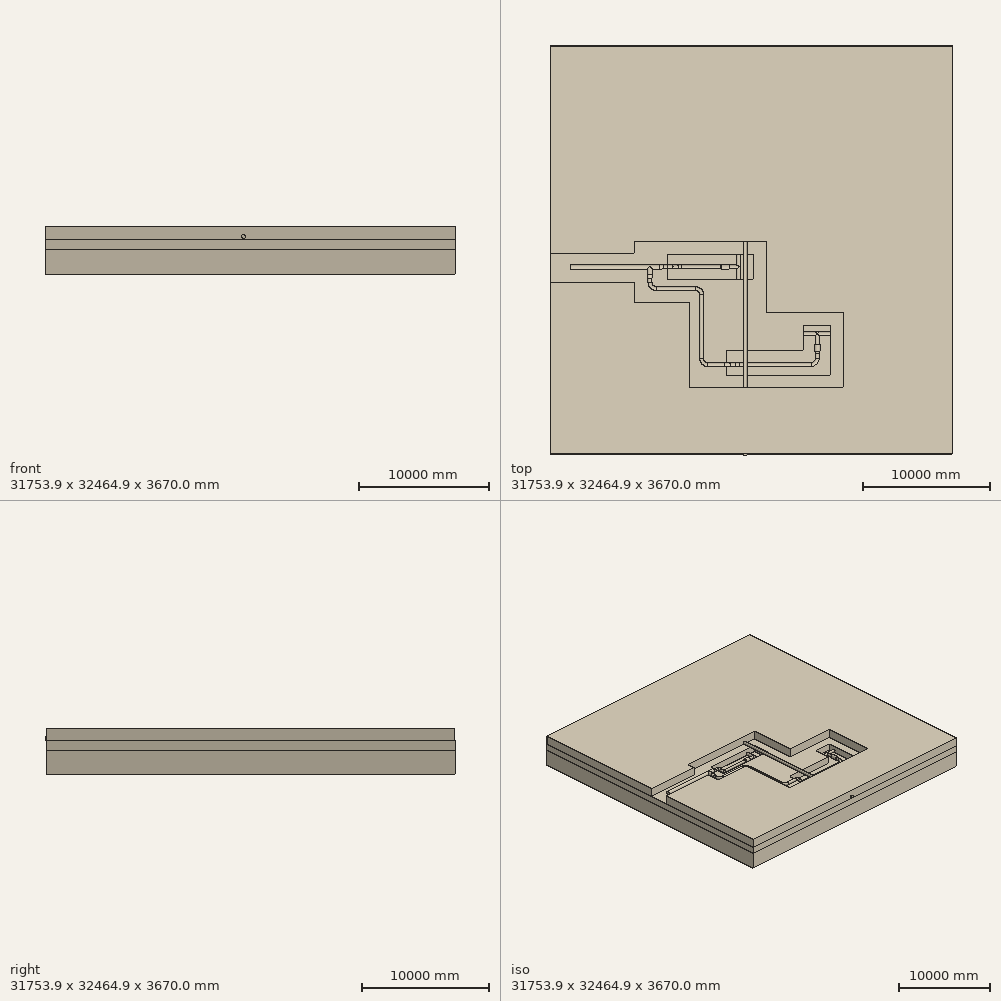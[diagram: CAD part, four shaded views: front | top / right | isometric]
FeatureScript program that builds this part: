
annotation { "Feature Type Name" : "Feature", "Feature Type Description" : "" }
export const myFeature = defineFeature(function(context is Context, id is Id, definition is map)
    precondition{}
    {
        {
            var Q0;
            Q0=qCreatedBy(makeId("Front.planeOp"),FACE);
            var sketch = newSketch(context, id + "F0", { "sketchPlane" : qUnion([Q0])});
            skCircle(sketch, "E0", {"center": v(0, 0) * mm, "radius": 157.5 * mm});
            skSolve(sketch);
        }
        {
            var Q0;
            Q0=qCreatedBy(makeId("Right.planeOp"),FACE);
            var sketch = newSketch(context, id + "F1", { "sketchPlane" : qUnion([Q0])});
            skLineSegment(sketch, "E1", {"start": v(0, 0) * mm, "end": v(-1158.97, 0) * mm});
            skLineSegment(sketch, "E2", {"start": v(-1512.52, -146.45) * mm, "end": v(-2019.63, -653.55) * mm});
            skLineSegment(sketch, "E3", {"start": v(-2373.18, -800) * mm, "end": v(-22166.07, -800) * mm});
            skPoint(sketch, "E4.visualSharp", {"position": v(-2166.07, -800) * mm});
            skArc(sketch, "E4.filletArc", {"start": v(-2373.18, -800) * mm, "mid": v(-2181.84, -761.94) * mm, "end": v(-2019.63, -653.55) * mm});
            skPoint(sketch, "E5.visualSharp", {"position": v(-1366.07, 0) * mm});
            skArc(sketch, "E5.filletArc", {"start": v(-1158.97, 0) * mm, "mid": v(-1350.3, -38.06) * mm, "end": v(-1512.52, -146.45) * mm});
            skSolve(sketch);
        }
        {
            var Q0;
            Q0=qSketchRegion(id+"F0",true);
            var Q1;
            Q1=qConstructionFilter(qBodyType(qCreatedBy(id+"F1",EDGE),BodyType.WIRE),ConstructionObject.NO);
            sweep(context, id + "F2", {"profiles" : qUnion([Q0]), "path" : qUnion([Q1])});
        }
        {
            var Q0;
            Q0=qCreatedBy(makeId("Front.planeOp"),FACE);
            var sketch = newSketch(context, id + "F3", { "sketchPlane" : qUnion([Q0])});
            skCircle(sketch, "E6", {"center": v(500, 0) * mm, "radius": 157.5 * mm});
            skSolve(sketch);
        }
        {
            var Q0;
            Q0=qSketchRegion(id+"F3",true);
            extrude(context, id + "F4", {"entities" : qUnion([Q0]), "depth" : 31800 * mm, "offsetDistance" : 25 * mm});
        }
        {
            var Q0;
            Q0=qCreatedBy(makeId("Right.planeOp"),FACE);
            var sketch = newSketch(context, id + "F5", { "sketchPlane" : qUnion([Q0])});
            skCircle(sketch, "E7", {"center": v(-22166, -800) * mm, "radius": 157.5 * mm});
            skSolve(sketch);
        }
        {
            var Q0;
            Q0=qCreatedBy(makeId("Right.planeOp"),FACE);
            cPlane(context, id + "F6", {"entities" : qUnion([Q0]), "cplaneType" : CPlaneType.OFFSET, "offset" : 16000 * mm, "width" : 150 * mm, "height" : 150 * mm});
        }
        {
            var Q0;
            Q0=qCreatedBy(id+"F6.planeOp",FACE);
            var sketch = newSketch(context, id + "F7", { "sketchPlane" : qUnion([Q0])});
            skCircle(sketch, "E8", {"center": v(-21525.22, 0) * mm, "radius": 157.5 * mm});
            skSolve(sketch);
        }
        {
            var Q0;
            Q0=qCreatedBy(makeId("Front.planeOp"),FACE);
            var Q1;
            Q1=sQuery(id+"F7.wireOp",VERTEX,"E8.center");
            cPlane(context, id + "F8", {"entities" : qUnion([Q0, Q1]), "cplaneType" : CPlaneType.PLANE_POINT, "offset" : 25 * mm, "width" : 150 * mm, "height" : 150 * mm});
        }
        {
            var Q0;
            Q0=qCreatedBy(id+"F8.planeOp",FACE);
            var sketch = newSketch(context, id + "F9", { "sketchPlane" : qUnion([Q0])});
            skLineSegment(sketch, "E9", {"start": v(16002.5, 0) * mm, "end": v(14288.3, 0) * mm});
            skLineSegment(sketch, "E10", {"start": v(13967.3, -116.64) * mm, "end": v(12326.43, -1490.56) * mm});
            skLineSegment(sketch, "E11", {"start": v(12005.44, -1607.2) * mm, "end": v(-8115.68, -1607.2) * mm});
            skLineSegment(sketch, "E12", {"start": v(-8532.64, -1383.14) * mm, "end": v(-9299.71, -224.06) * mm});
            skLineSegment(sketch, "E13", {"start": v(-9716.67, 0) * mm, "end": v(-13355.66, 0) * mm});
            skPoint(sketch, "E14.visualSharp", {"position": v(14106.6, 0) * mm});
            skArc(sketch, "E14.filletArc", {"start": v(14288.3, 0) * mm, "mid": v(14117.53, -30.06) * mm, "end": v(13967.3, -116.64) * mm});
            skPoint(sketch, "E15.visualSharp", {"position": v(12187.13, -1607.2) * mm});
            skArc(sketch, "E15.filletArc", {"start": v(12005.44, -1607.2) * mm, "mid": v(12176.2, -1577.13) * mm, "end": v(12326.43, -1490.56) * mm});
            skPoint(sketch, "E16.visualSharp", {"position": v(-9448, 0) * mm});
            skArc(sketch, "E16.filletArc", {"start": v(-9299.71, -224.06) * mm, "mid": v(-9480, -59.56) * mm, "end": v(-9716.67, 0) * mm});
            skPoint(sketch, "E17.visualSharp", {"position": v(-8384.36, -1607.2) * mm});
            skArc(sketch, "E17.filletArc", {"start": v(-8532.64, -1383.14) * mm, "mid": v(-8352.35, -1547.63) * mm, "end": v(-8115.68, -1607.2) * mm});
            skSolve(sketch);
        }
        {
            var Q0;
            Q0=qSketchRegion(id+"F7",true);
            var Q1;
            Q1=qConstructionFilter(qBodyType(qCreatedBy(id+"F9",EDGE),BodyType.WIRE),ConstructionObject.NO);
            sweep(context, id + "F10", {"profiles" : qUnion([Q0]), "path" : qUnion([Q1])});
        }
        {
            var Q0;
            Q0=qCreatedBy(id+"F6.planeOp",FACE);
            var sketch = newSketch(context, id + "F11", { "sketchPlane" : qUnion([Q0])});
            skCircle(sketch, "E18", {"center": v(-22166, 0) * mm, "radius": 157.5 * mm});
            skSolve(sketch);
        }
        {
            var Q0;
            Q0=qCreatedBy(makeId("Front.planeOp"),FACE);
            var Q1;
            Q1=sQuery(id+"F11.wireOp",VERTEX,"E18.center");
            cPlane(context, id + "F12", {"entities" : qUnion([Q0, Q1]), "cplaneType" : CPlaneType.PLANE_POINT, "offset" : 25 * mm, "width" : 150 * mm, "height" : 150 * mm});
        }
        {
            var Q0;
            Q0=qCreatedBy(id+"F12.planeOp",FACE);
            var sketch = newSketch(context, id + "F13", { "sketchPlane" : qUnion([Q0])});
            skLineSegment(sketch, "E19", {"start": v(16049.86, 0) * mm, "end": v(14213.99, 0) * mm});
            skLineSegment(sketch, "E20", {"start": v(13860.44, -146.45) * mm, "end": v(13353.33, -653.55) * mm});
            skLineSegment(sketch, "E21", {"start": v(12999.78, -800) * mm, "end": v(0, -800) * mm});
            skLineSegment(sketch, "E22", {"start": v(0, -800) * mm, "end": v(-8588.31, -800) * mm});
            skLineSegment(sketch, "E23", {"start": v(-8941.87, -653.55) * mm, "end": v(-9448.97, -146.45) * mm});
            skLineSegment(sketch, "E24", {"start": v(-9802.53, 0) * mm, "end": v(-13399.06, 0) * mm});
            skPoint(sketch, "E25.visualSharp", {"position": v(14006.88, 0) * mm});
            skArc(sketch, "E25.filletArc", {"start": v(14213.99, 0) * mm, "mid": v(14022.65, -38.06) * mm, "end": v(13860.44, -146.45) * mm});
            skPoint(sketch, "E26.visualSharp", {"position": v(13206.88, -800) * mm});
            skArc(sketch, "E26.filletArc", {"start": v(12999.78, -800) * mm, "mid": v(13191.12, -761.94) * mm, "end": v(13353.33, -653.55) * mm});
            skPoint(sketch, "E27.visualSharp", {"position": v(-8795.42, -800) * mm});
            skArc(sketch, "E27.filletArc", {"start": v(-8941.87, -653.55) * mm, "mid": v(-8779.66, -761.94) * mm, "end": v(-8588.31, -800) * mm});
            skPoint(sketch, "E28.visualSharp", {"position": v(-9595.42, 0) * mm});
            skArc(sketch, "E28.filletArc", {"start": v(-9448.97, -146.45) * mm, "mid": v(-9611.19, -38.06) * mm, "end": v(-9802.53, 0) * mm});
            skSolve(sketch);
        }
        {
            var Q0;
            Q0=qSketchRegion(id+"F11",true);
            var Q1;
            Q1=qConstructionFilter(qBodyType(qCreatedBy(id+"F13",EDGE),BodyType.WIRE),ConstructionObject.NO);
            sweep(context, id + "F14", {"operationType" : NewBodyOperationType.ADD, "profiles" : qUnion([Q0]), "path" : qUnion([Q1])});
        }
        {
            var Q0;
            Q0=makeQuery(id+"F10.opSweep","CAP_FACE",FACE,{"disambiguationData":[OSD([sQuery(id+"F7.wireOp",EDGE,"E8"),sQuery(id+"F9.wireOp",VERTEX,"E13.end")])],"isStart":true});
            var sketch = newSketch(context, id + "F15", { "sketchPlane" : qUnion([Q0])});
            skCircle(sketch, "E29", {"center": v(16867.72, 0) * mm, "radius": 225 * mm});
            skSolve(sketch);
        }
        {
            var Q0;
            Q0=qSketchRegion(id+"F15",true);
            extrude(context, id + "F16", {"entities" : qUnion([Q0]), "oppositeDirection" : true, "depth" : 7050 * mm, "offsetDistance" : 25 * mm});
        }
        {
            var Q0;
            Q0=makeQuery(id+"F16.opExtrude","CAP_FACE",FACE,{"disambiguationData":[OSD([sQuery(id+"F15.wireOp",EDGE,"E29")])],"isStart":false});
            var sketch = newSketch(context, id + "F17", { "sketchPlane" : qUnion([Q0])});
            skCircle(sketch, "E30", {"center": v(-16867.72, 0) * mm, "radius": 225 * mm});
            skSolve(sketch);
        }
        {
            var Q0;
            Q0=makeQuery(id+"F17.imprint","IMPRINT",FACE,{"disambiguationData":[TD([[makeQuery(id+"F17.imprint","IMPRINT",EDGE,{"derivedFrom":sQuery(id+"F17.wireOp",EDGE,"E30")}),-1.0]])]});
            cPlane(context, id + "F18", {"entities" : qUnion([Q0]), "cplaneType" : CPlaneType.OFFSET, "offset" : 343 * mm, "width" : 150 * mm, "height" : 150 * mm});
        }
        {
            var Q0;
            Q0=qCreatedBy(id+"F18.planeOp",FACE);
            var sketch = newSketch(context, id + "F19", { "sketchPlane" : qUnion([Q0])});
            skCircle(sketch, "E31", {"center": v(-16868.24, -67.5) * mm, "radius": 157.5 * mm});
            skSolve(sketch);
        }
        {
            var Q0;
            Q0=qSketchRegion(id+"F17",true);
            var Q1;
            Q1=qSketchRegion(id+"F19",true);
            loft(context, id + "F20", {"operationType" : NewBodyOperationType.ADD, "sheetProfilesArray" : [{ "sheetProfileEntities" : qUnion([Q0]) }, { "sheetProfileEntities" : qUnion([Q1]) }]});
        }
        {
            var Q0;
            Q0=qCreatedBy(makeId("Front.planeOp"),FACE);
            var Q1;
            Q1=sQuery(id+"F15.wireOp",VERTEX,"E29.center");
            cPlane(context, id + "F21", {"entities" : qUnion([Q0, Q1]), "cplaneType" : CPlaneType.PLANE_POINT, "offset" : 25 * mm, "width" : 150 * mm, "height" : 150 * mm});
        }
        {
            var Q0;
            Q0=qCreatedBy(id+"F21.planeOp",FACE);
            var sketch = newSketch(context, id + "F22", { "sketchPlane" : qUnion([Q0])});
            skLineSegment(sketch, "E32", {"start": v(-5962.66, -83.9) * mm, "end": v(-5669.76, -83.9) * mm});
            skLineSegment(sketch, "E33", {"start": v(-5316.21, -230.35) * mm, "end": v(-4893, -653.55) * mm});
            skLineSegment(sketch, "E34", {"start": v(-4539.45, -800) * mm, "end": v(-1450, -800) * mm});
            skPoint(sketch, "E35.visualSharp", {"position": v(-5462.66, -83.9) * mm});
            skArc(sketch, "E35.filletArc", {"start": v(-5316.21, -230.35) * mm, "mid": v(-5478.42, -121.96) * mm, "end": v(-5669.76, -83.9) * mm});
            skPoint(sketch, "E36.visualSharp", {"position": v(-4746.56, -800) * mm});
            skArc(sketch, "E36.filletArc", {"start": v(-4893, -653.55) * mm, "mid": v(-4730.8, -761.94) * mm, "end": v(-4539.45, -800) * mm});
            skSolve(sketch);
        }
        {
            var Q0;
            Q0=qSketchRegion(id+"F19",true);
            var Q1;
            Q1=qConstructionFilter(qBodyType(qCreatedBy(id+"F22",EDGE),BodyType.WIRE),ConstructionObject.NO);
            sweep(context, id + "F23", {"operationType" : NewBodyOperationType.ADD, "profiles" : qUnion([Q0]), "path" : qUnion([Q1])});
        }
        {
            var Q0;
            Q0=makeQuery(id+"F23.opSweep","CAP_FACE",FACE,{"disambiguationData":[OSD([sQuery(id+"F19.wireOp",EDGE,"E31"),sQuery(id+"F22.wireOp",VERTEX,"E34.end")])],"isStart":false});
            var sketch = newSketch(context, id + "F24", { "sketchPlane" : qUnion([Q0])});
            skCircle(sketch, "E37", {"center": v(-16868.24, -783.6) * mm, "radius": 157.5 * mm});
            skSolve(sketch);
        }
        {
            var Q0;
            Q0=qCreatedBy(makeId("Front.planeOp"),FACE);
            var Q1;
            Q1=sQuery(id+"F24.wireOp",VERTEX,"E37.center");
            cPlane(context, id + "F25", {"entities" : qUnion([Q0, Q1]), "cplaneType" : CPlaneType.PLANE_POINT, "offset" : 25 * mm, "width" : 150 * mm, "height" : 150 * mm});
        }
        {
            var Q0;
            Q0=qCreatedBy(id+"F25.planeOp",FACE);
            var sketch = newSketch(context, id + "F26", { "sketchPlane" : qUnion([Q0])});
            skCircle(sketch, "E38", {"center": v(-7026.1, 0) * mm, "radius": 225 * mm});
            skSolve(sketch);
        }
        {
            var Q0;
            Q0=qSketchRegion(id+"F26",true);
            extrude(context, id + "F27", {"entities" : qUnion([Q0]), "operationType" : NewBodyOperationType.ADD, "depth" : 610 * mm, "offsetDistance" : 25 * mm});
        }
        {
            var Q0;
            Q0=makeQuery(id+"F27.opExtrude","CAP_FACE",FACE,{"disambiguationData":[OSD([sQuery(id+"F26.wireOp",EDGE,"E38")])],"isStart":false});
            var sketch = newSketch(context, id + "F28", { "sketchPlane" : qUnion([Q0])});
            skCircle(sketch, "E39", {"center": v(-7026.1, 0) * mm, "radius": 225 * mm});
            skSolve(sketch);
        }
        {
            var Q0;
            Q0=makeQuery(id+"F28.imprint","IMPRINT",FACE,{"disambiguationData":[TD([[makeQuery(id+"F28.imprint","IMPRINT",EDGE,{"derivedFrom":sQuery(id+"F28.wireOp",EDGE,"E39")}),1.0]])]});
            cPlane(context, id + "F29", {"entities" : qUnion([Q0]), "cplaneType" : CPlaneType.OFFSET, "offset" : 300 * mm, "width" : 150 * mm, "height" : 150 * mm});
        }
        {
            var Q0;
            Q0=qCreatedBy(id+"F29.planeOp",FACE);
            var sketch = newSketch(context, id + "F30", { "sketchPlane" : qUnion([Q0])});
            skCircle(sketch, "E40", {"center": v(-7026.1, -68) * mm, "radius": 157.5 * mm});
            skSolve(sketch);
        }
        {
            var Q0;
            Q0=qSketchRegion(id+"F28",true);
            var Q1;
            Q1=qSketchRegion(id+"F30",true);
            loft(context, id + "F31", {"operationType" : NewBodyOperationType.ADD, "sheetProfilesArray" : [{ "sheetProfileEntities" : qUnion([Q0]) }, { "sheetProfileEntities" : qUnion([Q1]) }]});
        }
        {
            var Q0;
            Q0=qCreatedBy(id+"F29.planeOp",FACE);
            var sketch = newSketch(context, id + "F32", { "sketchPlane" : qUnion([Q0])});
            skCircle(sketch, "E41", {"center": v(-7028.94, -67.68) * mm, "radius": 157.5 * mm});
            skSolve(sketch);
        }
        {
            var Q0;
            Q0=makeQuery(id+"F31.opLoft","CAP_FACE",FACE,{"disambiguationData":[OSD([makeQuery(id+"F30.imprint","IMPRINT",FACE,{"disambiguationData":[TD([[makeQuery(id+"F30.imprint","IMPRINT",EDGE,{"derivedFrom":sQuery(id+"F30.wireOp",EDGE,"E40")}),1.0]])]})])],"isStart":true});
            var sketch = newSketch(context, id + "F33", { "sketchPlane" : qUnion([Q0])});
            skCircle(sketch, "E42", {"center": v(-7027.04, -67.76) * mm, "radius": 157.5 * mm});
            skSolve(sketch);
        }
        {
            var Q0;
            Q0=qCreatedBy(makeId("Top.planeOp"),FACE);
            var Q1;
            Q1=sQuery(id+"F33.wireOp",VERTEX,"E42.center");
            cPlane(context, id + "F34", {"entities" : qUnion([Q0, Q1]), "cplaneType" : CPlaneType.PLANE_POINT, "offset" : 25 * mm, "width" : 150 * mm, "height" : 150 * mm});
        }
        {
            var Q0;
            Q0=qCreatedBy(id+"F34.planeOp",FACE);
            var sketch = newSketch(context, id + "F35", { "sketchPlane" : qUnion([Q0])});
            skLineSegment(sketch, "E43", {"start": v(-7027.04, -17778.24) * mm, "end": v(-7027.04, -18080.14) * mm});
            skLineSegment(sketch, "E44", {"start": v(-6527.04, -18580.14) * mm, "end": v(-3436.34, -18580.14) * mm});
            skLineSegment(sketch, "E45", {"start": v(-2936.34, -19080.14) * mm, "end": v(-2936.34, -23104.43) * mm});
            skPoint(sketch, "E46.visualSharp", {"position": v(-7027.04, -18580.14) * mm});
            skArc(sketch, "E46.filletArc", {"start": v(-7027.04, -18080.14) * mm, "mid": v(-6880.6, -18433.69) * mm, "end": v(-6527.04, -18580.14) * mm});
            skPoint(sketch, "E47.visualSharp", {"position": v(-2936.34, -18580.14) * mm});
            skArc(sketch, "E47.filletArc", {"start": v(-2936.34, -19080.14) * mm, "mid": v(-3082.79, -18726.58) * mm, "end": v(-3436.34, -18580.14) * mm});
            skSolve(sketch);
        }
        {
            var Q0;
            Q0 = qSketchRegion(id + "F33", true);
            var Q1;
            Q1 = qConstructionFilter(qBodyType(qCreatedBy(id + "F35" ,EDGE), BodyType.WIRE), ConstructionObject.NO);
            sweep(context, id + "F36", {"operationType" : NewBodyOperationType.ADD, "profiles" : qUnion([Q0]), "path" : qUnion([Q1])});
        }
        {
            var Q0;
            Q0=qCreatedBy(makeId("Top.planeOp"),FACE);
            var Q1;
            Q1=sQuery(id+"F32.wireOp",VERTEX,"E41.center");
            cPlane(context, id + "F37", {"entities" : qUnion([Q0, Q1]), "cplaneType" : CPlaneType.PLANE_POINT, "offset" : 25 * mm, "width" : 150 * mm, "height" : 150 * mm});
        }
        {
            var Q0;
            Q0=qCreatedBy(id+"F37.planeOp",FACE);
            var sketch = newSketch(context, id + "F38", { "sketchPlane" : qUnion([Q0])});
            skLineSegment(sketch, "E48", {"start": v(-2933.83, -23104.43) * mm, "end": v(-2933.83, -24104.43) * mm});
            skLineSegment(sketch, "E49", {"start": v(-2433.83, -24604.43) * mm, "end": v(-1452.2, -24604.43) * mm});
            skPoint(sketch, "E50.visualSharp", {"position": v(-2952.2, -24604.31) * mm});
            skArc(sketch, "E50.filletArc", {"start": v(-2933.83, -24104.43) * mm, "mid": v(-2787.38, -24457.98) * mm, "end": v(-2433.83, -24604.43) * mm});
            skSolve(sketch);
        }
        {
            var Q0;
            Q0=makeQuery(id+"F36.opSweep","CAP_FACE",FACE,{"disambiguationData":[OSD([sQuery(id+"F33.wireOp",EDGE,"E42"),sQuery(id+"F35.wireOp",VERTEX,"E45.end")])],"isStart":false});
            var sketch = newSketch(context, id + "F39", { "sketchPlane" : qUnion([Q0])});
            skCircle(sketch, "E51", {"center": v(-2936.34, -67.76) * mm, "radius": 157.5 * mm});
            skSolve(sketch);
        }
        {
            var Q0;
            Q0=qSketchRegion(id+"F39",true);
            var Q1;
            Q1=qConstructionFilter(qBodyType(qCreatedBy(id+"F38",EDGE),BodyType.WIRE),ConstructionObject.NO);
            sweep(context, id + "F40", {"operationType" : NewBodyOperationType.ADD, "profiles" : qUnion([Q0]), "path" : qUnion([Q1])});
        }
        {
            var Q0;
            Q0=makeQuery(id+"F40.opSweep","CAP_FACE",FACE,{"disambiguationData":[OSD([sQuery(id+"F38.wireOp",VERTEX,"E49.end"),sQuery(id+"F39.wireOp",EDGE,"pikIjlxL-Iweg-K63M-rDVM-WGOUHQlHPGsE")])],"isStart":false});
            var sketch = newSketch(context, id + "F41", { "sketchPlane" : qUnion([Q0])});
            skCircle(sketch, "E52", {"center": v(-24606.94, -67.76) * mm, "radius": 157.5 * mm});
            skSolve(sketch);
        }
        {
            var Q0;
            Q0=qCreatedBy(makeId("Top.planeOp"),FACE);
            var Q1;
            Q1=sQuery(id+"F41.wireOp",VERTEX,"E52.center");
            cPlane(context, id + "F42", {"entities" : qUnion([Q0, Q1]), "cplaneType" : CPlaneType.PLANE_POINT, "offset" : 25 * mm, "width" : 150 * mm, "height" : 150 * mm});
        }
        {
            var Q0;
            Q0=qCreatedBy(makeId("Front.planeOp"),FACE);
            var Q1;
            Q1=sQuery(id+"F41.wireOp",VERTEX,"E52.center");
            cPlane(context, id + "F43", {"entities" : qUnion([Q0, Q1]), "cplaneType" : CPlaneType.PLANE_POINT, "offset" : 25 * mm, "width" : 150 * mm, "height" : 150 * mm});
        }
        {
            var Q0;
            Q0=qCreatedBy(id+"F43.planeOp",FACE);
            var sketch = newSketch(context, id + "F44", { "sketchPlane" : qUnion([Q0])});
            skLineSegment(sketch, "E53", {"start": v(-1452.2, -67.68) * mm, "end": v(-1121.65, -67.68) * mm});
            skLineSegment(sketch, "E54", {"start": v(-768.1, -214.12) * mm, "end": v(-328.66, -653.55) * mm});
            skLineSegment(sketch, "E55", {"start": v(24.9, -800) * mm, "end": v(4519.07, -800) * mm});
            skPoint(sketch, "E56.visualSharp", {"position": v(-914.54, -67.68) * mm});
            skArc(sketch, "E56.filletArc", {"start": v(-768.1, -214.12) * mm, "mid": v(-930.3, -105.74) * mm, "end": v(-1121.65, -67.68) * mm});
            skPoint(sketch, "E57.visualSharp", {"position": v(-182.22, -800) * mm});
            skArc(sketch, "E57.filletArc", {"start": v(-328.66, -653.55) * mm, "mid": v(-166.45, -761.94) * mm, "end": v(24.9, -800) * mm});
            skSolve(sketch);
        }
        {
            var Q0;
            Q0=qSketchRegion(id+"F41",true);
            var Q1;
            Q1=qConstructionFilter(qBodyType(qCreatedBy(id+"F44",EDGE),BodyType.WIRE),ConstructionObject.NO);
            sweep(context, id + "F45", {"operationType" : NewBodyOperationType.ADD, "profiles" : qUnion([Q0]), "path" : qUnion([Q1])});
        }
        {
            var Q0;
            Q0=makeQuery(id+"F45.opSweep","CAP_FACE",FACE,{"disambiguationData":[OSD([sQuery(id+"F41.wireOp",EDGE,"E52"),sQuery(id+"F44.wireOp",VERTEX,"E55.end")])],"isStart":false});
            var sketch = newSketch(context, id + "F46", { "sketchPlane" : qUnion([Q0])});
            skCircle(sketch, "E58", {"center": v(-24606.94, -800.08) * mm, "radius": 157.5 * mm});
            skSolve(sketch);
        }
        {
            var Q0;
            Q0=qCreatedBy(makeId("Top.planeOp"),FACE);
            var Q1;
            Q1=sQuery(id+"F46.wireOp",VERTEX,"E58.center");
            cPlane(context, id + "F47", {"entities" : qUnion([Q0, Q1]), "cplaneType" : CPlaneType.PLANE_POINT, "offset" : 25 * mm, "width" : 150 * mm, "height" : 150 * mm});
        }
        {
            var Q0;
            Q0=qCreatedBy(id+"F47.planeOp",FACE);
            var sketch = newSketch(context, id + "F48", { "sketchPlane" : qUnion([Q0])});
            skLineSegment(sketch, "E59", {"start": v(4519.07, -24606.94) * mm, "end": v(5727.78, -24606.94) * mm});
            skLineSegment(sketch, "E60", {"start": v(6227.78, -24106.94) * mm, "end": v(6227.78, -23690.58) * mm});
            skPoint(sketch, "E61.visualSharp", {"position": v(6227.78, -24606.94) * mm});
            skArc(sketch, "E61.filletArc", {"start": v(5727.78, -24606.94) * mm, "mid": v(6081.34, -24460.5) * mm, "end": v(6227.78, -24106.94) * mm});
            skSolve(sketch);
        }
        {
            var Q0;
            Q0=qSketchRegion(id+"F46",true);
            var Q1;
            Q1=qConstructionFilter(qBodyType(qCreatedBy(id+"F48",EDGE),BodyType.WIRE),ConstructionObject.NO);
            sweep(context, id + "F49", {"operationType" : NewBodyOperationType.ADD, "profiles" : qUnion([Q0]), "path" : qUnion([Q1])});
        }
        {
            var Q0;
            Q0=makeQuery(id+"F24.imprint","IMPRINT",FACE,{"disambiguationData":[TD([[makeQuery(id+"F24.imprint","IMPRINT",EDGE,{"derivedFrom":sQuery(id+"F24.wireOp",EDGE,"E37")}),1.0]])]});
            var sketch = newSketch(context, id + "F50", { "sketchPlane" : qUnion([Q0])});
            skCircle(sketch, "E62", {"center": v(-16868.23, -783.6) * mm, "radius": 157.5 * mm});
            skSolve(sketch);
        }
        {
            var Q0;
            Q0=qSketchRegion(id+"F50",true);
            extrude(context, id + "F51", {"entities" : qUnion([Q0]), "depth" : 120 * mm, "offsetDistance" : 25 * mm});
        }
        {
            var Q0;
            Q0=makeQuery(id+"F51.opExtrude","CAP_FACE",FACE,{"disambiguationData":[OSD([sQuery(id+"F50.wireOp",EDGE,"E62")])],"isStart":false});
            var sketch = newSketch(context, id + "F52", { "sketchPlane" : qUnion([Q0])});
            skCircle(sketch, "E63", {"center": v(-16868.23, -783.6) * mm, "radius": 225 * mm});
            skSolve(sketch);
        }
        {
            var Q0;
            Q0=qSketchRegion(id+"F52",true);
            extrude(context, id + "F53", {"entities" : qUnion([Q0]), "operationType" : NewBodyOperationType.ADD, "depth" : 610 * mm, "offsetDistance" : 25 * mm});
        }
        {
            var Q0;
            Q0=makeQuery(id+"F53.opExtrude","CAP_FACE",FACE,{"disambiguationData":[OSD([sQuery(id+"F52.wireOp",EDGE,"E63")])],"isStart":false});
            var sketch = newSketch(context, id + "F54", { "sketchPlane" : qUnion([Q0])});
            skCircle(sketch, "E64", {"center": v(-16868.23, -783.6) * mm, "radius": 157.5 * mm});
            skSolve(sketch);
        }
        {
            var Q0;
            Q0=qSketchRegion(id+"F54",true);
            var Q1;
            {var subQ0=sQuery(id+"F0.wireOp",EDGE,"E0");var subQ1=makeQuery(id+"F2.opSweep","SWEPT_FACE",FACE,{"disambiguationData":[OSD([subQ0,sQuery(id+"F1.wireOp",EDGE,"E3")])]});Q1=makeQuery(id+"F14.boolean.opBoolean","SPLIT",FACE,{"disambiguationData":[TD([subQ1,makeQuery(id+"F2.opSweep","SWEPT_FACE",FACE,{"disambiguationData":[OSD([subQ0,sQuery(id+"F1.wireOp",EDGE,"E4.filletArc")])]}),makeQuery(id+"F14.opSweep","SWEPT_FACE",FACE,{"disambiguationData":[OSD([sQuery(id+"F11.wireOp",EDGE,"E18"),sQuery(id+"F13.wireOp",EDGE,"E22")])]})])],"derivedFrom":subQ1});}
            extrude(context, id + "F55", {"entities" : qUnion([Q0]), "depth" : 770 * mm, "endBoundEntityFace" : qUnion([Q1]), "offsetDistance" : 25 * mm});
        }
        {
            var Q0;
            Q0=qCreatedBy(makeId("Top.planeOp"),FACE);
            cPlane(context, id + "F56", {"entities" : qUnion([Q0]), "cplaneType" : CPlaneType.OFFSET, "offset" : 2900 * mm, "oppositeDirection" : true, "width" : 150 * mm, "height" : 150 * mm});
        }
        {
            var Q0;
            Q0=qCreatedBy(id+"F56.planeOp",FACE);
            var sketch = newSketch(context, id + "F57", { "sketchPlane" : qUnion([Q0])});
            skLineSegment(sketch, "E65.bottom", {"start": v(-14864.21, 664.91) * mm, "end": v(16889.7, 664.91) * mm});
            skLineSegment(sketch, "E65.top", {"start": v(-14864.21, -31680.33) * mm, "end": v(16889.7, -31680.33) * mm});
            skLineSegment(sketch, "E65.left", {"start": v(-14864.21, 664.91) * mm, "end": v(-14864.21, -31680.33) * mm});
            skLineSegment(sketch, "E65.right", {"start": v(16889.7, 664.91) * mm, "end": v(16889.7, -31680.33) * mm});
            skSolve(sketch);
        }
        {
            var Q0;
            Q0=makeQuery(id+"F49.opSweep","CAP_FACE",FACE,{"disambiguationData":[OSD([sQuery(id+"F46.wireOp",EDGE,"E58"),sQuery(id+"F48.wireOp",VERTEX,"E60.end")])],"isStart":false});
            var sketch = newSketch(context, id + "F58", { "sketchPlane" : qUnion([Q0])});
            skCircle(sketch, "E66", {"center": v(-6227.78, -800.08) * mm, "radius": 157.5 * mm});
            skSolve(sketch);
        }
        {
            var Q0;
            Q0=qSketchRegion(id+"F58",true);
            extrude(context, id + "F59", {"entities" : qUnion([Q0]), "depth" : 110 * mm, "offsetDistance" : 25 * mm});
        }
        {
            var Q0;
            Q0=makeQuery(id+"F59.opExtrude","CAP_FACE",FACE,{"disambiguationData":[OSD([sQuery(id+"F58.wireOp",EDGE,"E66")])],"isStart":false});
            var sketch = newSketch(context, id + "F60", { "sketchPlane" : qUnion([Q0])});
            skCircle(sketch, "E67", {"center": v(-6227.78, -800.08) * mm, "radius": 225 * mm});
            skSolve(sketch);
        }
        {
            var Q0;
            Q0=qSketchRegion(id+"F60",true);
            extrude(context, id + "F61", {"entities" : qUnion([Q0]), "operationType" : NewBodyOperationType.ADD, "depth" : 560 * mm, "offsetDistance" : 25 * mm});
        }
        {
            var Q0;
            Q0=makeQuery(id+"F61.opExtrude","CAP_FACE",FACE,{"disambiguationData":[OSD([sQuery(id+"F60.wireOp",EDGE,"E67")])],"isStart":false});
            var sketch = newSketch(context, id + "F62", { "sketchPlane" : qUnion([Q0])});
            skCircle(sketch, "E68", {"center": v(-6227.78, -800.08) * mm, "radius": 157.5 * mm});
            skSolve(sketch);
        }
        {
            var Q0;
            Q0=qSketchRegion(id+"F62",true);
            extrude(context, id + "F63", {"entities" : qUnion([Q0]), "depth" : 1000 * mm, "offsetDistance" : 25 * mm});
        }
        {
            var Q0;
            Q0=qSketchRegion(id+"F57",true);
            extrude(context, id + "F64", {"entities" : qUnion([Q0]), "depth" : 1890 * mm, "offsetDistance" : 25 * mm});
        }
        {
            var Q0;
            Q0=makeQuery(id+"F64.opExtrude","CAP_FACE",FACE,{"disambiguationData":[OSD([sQuery(id+"F57.wireOp",EDGE,"E65.bottom"),sQuery(id+"F57.wireOp",EDGE,"E65.top"),sQuery(id+"F57.wireOp",EDGE,"E65.left"),sQuery(id+"F57.wireOp",EDGE,"E65.right")])],"isStart":false});
            var sketch = newSketch(context, id + "F65", { "sketchPlane" : qUnion([Q0])});
            skLineSegment(sketch, "E69.bottom", {"start": v(-14864.21, 664.91) * mm, "end": v(16889.7, 664.91) * mm});
            skLineSegment(sketch, "E69.top", {"start": v(-5631.58, -15868.24) * mm, "end": v(1180.23, -15868.24) * mm});
            skLineSegment(sketch, "E69.left", {"start": v(-14864.21, 664.91) * mm, "end": v(-14864.21, -15868.24) * mm});
            skLineSegment(sketch, "E69.right", {"start": v(16889.7, 664.91) * mm, "end": v(16889.7, -15868.24) * mm});
            skLineSegment(sketch, "E70.top", {"start": v(-14864.21, -31680.33) * mm, "end": v(16889.7, -31680.33) * mm});
            skLineSegment(sketch, "E70.left", {"start": v(-14864.21, -15868.24) * mm, "end": v(-14864.21, -31680.33) * mm});
            skLineSegment(sketch, "E70.right", {"start": v(16889.7, -15868.24) * mm, "end": v(16889.7, -31680.33) * mm});
            skLineSegment(sketch, "E71.trimOffspring", {"start": v(-5631.58, -17868.24) * mm, "end": v(1180.23, -17868.24) * mm});
            skLineSegment(sketch, "E72", {"start": v(-5631.58, -17868.24) * mm, "end": v(-5631.58, -15868.24) * mm});
            skLineSegment(sketch, "E73", {"start": v(1180.23, -17868.24) * mm, "end": v(1180.23, -15868.24) * mm});
            skLineSegment(sketch, "E74", {"start": v(-959.4, -23455.96) * mm, "end": v(-959.4, -25443.46) * mm});
            skLineSegment(sketch, "E75", {"start": v(-959.4, -25443.46) * mm, "end": v(7277.1, -25443.46) * mm});
            skLineSegment(sketch, "E76", {"start": v(7277.1, -25443.46) * mm, "end": v(7277.1, -21468.46) * mm});
            skLineSegment(sketch, "E77", {"start": v(7277.1, -21468.46) * mm, "end": v(5092.63, -21468.46) * mm});
            skLineSegment(sketch, "E78", {"start": v(5092.63, -21468.46) * mm, "end": v(5092.63, -23455.96) * mm});
            skLineSegment(sketch, "E79", {"start": v(5092.63, -23455.96) * mm, "end": v(-959.4, -23455.96) * mm});
            skSolve(sketch);
        }
        {
            var Q0;
            Q0=qSketchRegion(id+"F65",true);
            extrude(context, id + "F66", {"entities" : qUnion([Q0]), "depth" : 780 * mm, "offsetDistance" : 25 * mm});
        }
        {
            var Q0;
            Q0=makeQuery(id+"F66.opExtrude","CAP_FACE",FACE,{"disambiguationData":[OSD([sQuery(id+"F65.wireOp",EDGE,"E69.bottom"),sQuery(id+"F65.wireOp",EDGE,"E69.top"),sQuery(id+"F65.wireOp",EDGE,"E69.left"),sQuery(id+"F65.wireOp",EDGE,"E69.right"),sQuery(id+"F65.wireOp",EDGE,"E70.top"),sQuery(id+"F65.wireOp",EDGE,"E70.left"),sQuery(id+"F65.wireOp",EDGE,"E70.right"),sQuery(id+"F65.wireOp",EDGE,"cZdsMfuH-jNO2-9ODL-juzj-WbjWhcxb1HZy.bottom"),sQuery(id+"F65.wireOp",EDGE,"cZdsMfuH-jNO2-9ODL-juzj-WbjWhcxb1HZy.right"),sQuery(id+"F65.wireOp",EDGE,"woFda3sP-0efr-ts02-7ppw-0Dkzhy5AtgHi.bottom"),sQuery(id+"F65.wireOp",EDGE,"woFda3sP-0efr-ts02-7ppw-0Dkzhy5AtgHi.left"),sQuery(id+"F65.wireOp",EDGE,"woFda3sP-0efr-ts02-7ppw-0Dkzhy5AtgHi.right"),sQuery(id+"F65.wireOp",EDGE,"ba6e1593-ac43-4f9c-a249-e36eadffeca0.trimOffspring"),sQuery(id+"F65.wireOp",EDGE,"E71.trimOffspring"),sQuery(id+"F65.wireOp",EDGE,"q2DGIA3x-tNrC-QMrD-Nkjg-5i6079NTCb2X"),sQuery(id+"F65.wireOp",EDGE,"c0bdaf5c-f50e-415c-9e35-08e7864d3955.trimOffspring"),sQuery(id+"F65.wireOp",EDGE,"E72"),sQuery(id+"F65.wireOp",EDGE,"E73")])],"isStart":false});
            var sketch = newSketch(context, id + "F67", { "sketchPlane" : qUnion([Q0])});
            skLineSegment(sketch, "E80.bottom", {"start": v(-14864.21, 583.74) * mm, "end": v(16889.7, 583.74) * mm});
            skLineSegment(sketch, "E80.top", {"start": v(-8262.13, -14868.24) * mm, "end": v(2180.23, -14868.24) * mm});
            skLineSegment(sketch, "E80.left", {"start": v(-14864.21, 583.74) * mm, "end": v(-14864.21, -15805.74) * mm});
            skLineSegment(sketch, "E80.right", {"start": v(16889.7, 583.74) * mm, "end": v(16889.7, -14868.24) * mm});
            skLineSegment(sketch, "E81.bottom", {"start": v(-14864.21, -18097.1) * mm, "end": v(-8262.13, -18097.1) * mm});
            skLineSegment(sketch, "E81.left", {"start": v(-14864.21, -18097.1) * mm, "end": v(-14864.21, -26443.46) * mm});
            skLineSegment(sketch, "E82", {"start": v(-8262.13, -18097.1) * mm, "end": v(-8262.13, -19647.5) * mm});
            skLineSegment(sketch, "E83.bottom", {"start": v(-14864.21, -31680.33) * mm, "end": v(16889.7, -31680.33) * mm});
            skLineSegment(sketch, "E83.top", {"start": v(-14864.21, -26443.46) * mm, "end": v(8277.1, -26443.46) * mm});
            skLineSegment(sketch, "E83.left", {"start": v(-14864.21, -31680.33) * mm, "end": v(-14864.21, -26443.46) * mm});
            skLineSegment(sketch, "E83.right", {"start": v(16889.7, -31680.33) * mm, "end": v(16889.7, -26594.84) * mm});
            skLineSegment(sketch, "E84.left", {"start": v(16889.7, -14868.24) * mm, "end": v(16889.7, -27043.92) * mm});
            skLineSegment(sketch, "E84.right", {"start": v(8277.1, -20468.46) * mm, "end": v(8277.1, -26443.46) * mm});
            skLineSegment(sketch, "E85.top", {"start": v(2180.23, -20468.46) * mm, "end": v(8277.1, -20468.46) * mm});
            skLineSegment(sketch, "E85.left", {"start": v(2180.23, -14868.24) * mm, "end": v(2180.23, -20468.46) * mm});
            skLineSegment(sketch, "E86.top", {"start": v(-8262.13, -15805.74) * mm, "end": v(-14864.21, -15805.74) * mm});
            skLineSegment(sketch, "E86.left", {"start": v(-8262.13, -14868.24) * mm, "end": v(-8262.13, -15805.74) * mm});
            skLineSegment(sketch, "E87.bottom", {"start": v(-8262.13, -19647.5) * mm, "end": v(-3899.82, -19647.5) * mm});
            skLineSegment(sketch, "E87.right", {"start": v(-3899.82, -19647.5) * mm, "end": v(-3899.82, -26443.46) * mm});
            skSolve(sketch);
        }
        {
            var Q0;
            Q0=qSketchRegion(id+"F67",true);
            extrude(context, id + "F68", {"entities" : qUnion([Q0]), "depth" : 1000 * mm, "offsetDistance" : 25 * mm});
        }
    });
